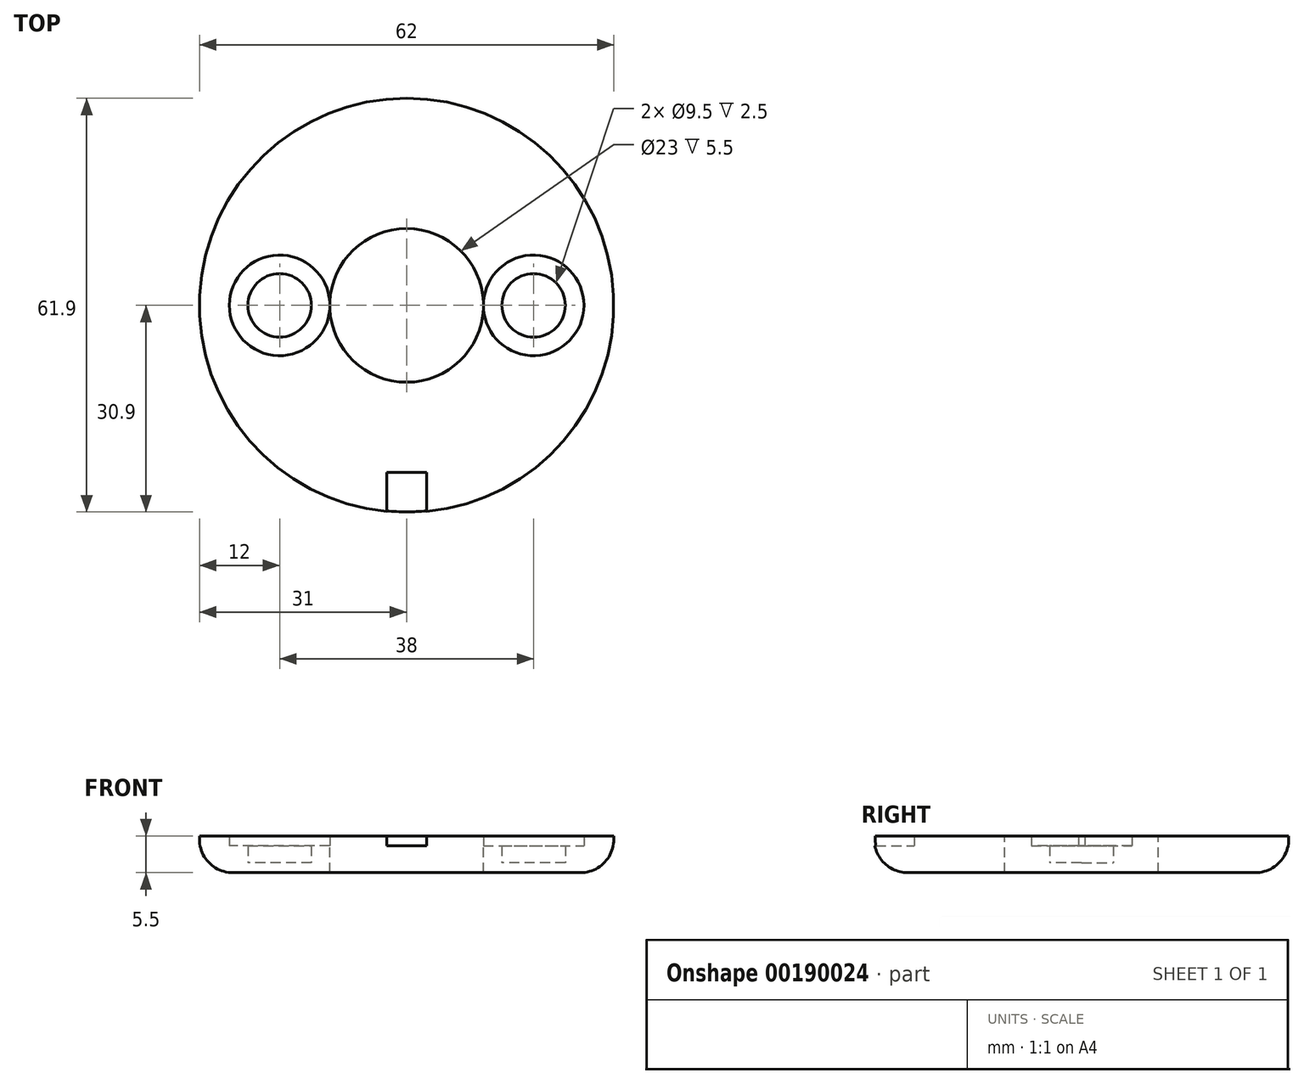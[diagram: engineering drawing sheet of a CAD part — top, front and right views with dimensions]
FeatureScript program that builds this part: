
annotation { "Feature Type Name" : "Feature", "Feature Type Description" : "" }
export const myFeature = defineFeature(function(context is Context, id is Id, definition is map)
    precondition{}
    {
        {
            var Q0;
            Q0=qCreatedBy(makeId("Top.planeOp"),FACE);
            var sketch = newSketch(context, id + "F0", { "sketchPlane" : qUnion([Q0])});
            skCircle(sketch, "E0", {"center": v(0, 0) * mm, "radius": 31 * mm});
            skLineSegment(sketch, "E1", {"start": v(-31, 0) * mm, "end": v(31, 0) * mm, "construction": true});
            skCircle(sketch, "E2", {"center": v(0, 0) * mm, "radius": 11.5 * mm});
            skSolve(sketch);
        }
        {
            var Q0;
            Q0=makeQuery(id+"F0.imprint","IMPRINT",FACE,{"disambiguationData":[TD([[makeQuery(id+"F0.imprint","IMPRINT",EDGE,{"derivedFrom":sQuery(id+"F0.wireOp",EDGE,"E0")}),1.0]])]});
            extrude(context, id + "F1", {"entities" : qUnion([Q0]), "oppositeDirection" : true, "depth" : 1.5 * mm});
        }
        {
            var Q0;
            Q0=makeQuery(id+"F1.opExtrude","CAP_FACE",FACE,{"disambiguationData":[OSD([sQuery(id+"F0.wireOp",EDGE,"E0"),sQuery(id+"F0.wireOp",EDGE,"E2")])],"isStart":false});
            var sketch = newSketch(context, id + "F2", { "sketchPlane" : qUnion([Q0])});
            skCircle(sketch, "E3.0", {"center": v(0, 0) * mm, "radius": 31 * mm});
            skCircle(sketch, "E4.0", {"center": v(0, 0) * mm, "radius": 11.5 * mm});
            skLineSegment(sketch, "E5.0", {"start": v(-31, 0) * mm, "end": v(31, 0) * mm, "construction": true});
            skPoint(sketch, "E6", {"position": v(-19, 0) * mm});
            skPoint(sketch, "E7", {"position": v(19, 0) * mm});
            skCircle(sketch, "E8", {"center": v(19, 0) * mm, "radius": 4.75 * mm});
            skCircle(sketch, "E9", {"center": v(-19, 0) * mm, "radius": 4.75 * mm});
            skSolve(sketch);
        }
        {
            var Q0;
            Q0=makeQuery(id+"F2.imprint","IMPRINT",FACE,{"disambiguationData":[TD([[makeQuery(id+"F2.imprint","IMPRINT",EDGE,{"derivedFrom":sQuery(id+"F2.wireOp",EDGE,"E3.0")}),-1.0]])]});
            extrude(context, id + "F3", {"entities" : qUnion([Q0]), "operationType" : NewBodyOperationType.ADD, "oppositeDirection" : true, "depth" : 4 * mm});
        }
        {
            var Q0;
            Q0=makeQuery(id+"F3.opExtrude","CAP_FACE",FACE,{"disambiguationData":[OSD([sQuery(id+"F2.wireOp",EDGE,"E3.0"),sQuery(id+"F2.wireOp",EDGE,"E4.0"),sQuery(id+"F2.wireOp",EDGE,"E8"),sQuery(id+"F2.wireOp",EDGE,"E9")])],"isStart":false});
            var sketch = newSketch(context, id + "F4", { "sketchPlane" : qUnion([Q0])});
            skCircle(sketch, "E10.0", {"center": v(0, 0) * mm, "radius": 31 * mm});
            skCircle(sketch, "E11.0", {"center": v(0, 0) * mm, "radius": 11.5 * mm});
            skPoint(sketch, "E12.0", {"position": v(-19, 0) * mm});
            skPoint(sketch, "E13.0", {"position": v(19, 0) * mm});
            skCircle(sketch, "E14", {"center": v(19, 0) * mm, "radius": 7.53 * mm});
            skCircle(sketch, "E15", {"center": v(-19, 0) * mm, "radius": 7.53 * mm});
            skLineSegment(sketch, "E16", {"start": v(0, 0) * mm, "end": v(0, -31) * mm, "construction": true});
            skLineSegment(sketch, "E17", {"start": v(-3, -30.85) * mm, "end": v(-3, -25) * mm});
            skLineSegment(sketch, "E18", {"start": v(-3, -25) * mm, "end": v(3, -25) * mm});
            skLineSegment(sketch, "E19", {"start": v(3, -25) * mm, "end": v(3, -30.85) * mm});
            skSolve(sketch);
        }
        {
            var Q0;
            {var subQ5=sQuery(id+"F4.wireOp",EDGE,"E17");Q0=makeQuery(id+"F4.imprint","IMPRINT",FACE,{"disambiguationData":[TD([[makeQuery(id+"F4.imprint","IMPRINT",EDGE,{"derivedFrom":subQ5}),1.0]])]});}
            extrude(context, id + "F5", {"entities" : qUnion([Q0]), "operationType" : NewBodyOperationType.ADD, "depth" : 1.5 * mm});
        }
        {
            var Q0;
            Q0=makeQuery(id+"F1.opExtrude","CAP_EDGE",EDGE,{"disambiguationData":[OSD([sQuery(id+"F0.wireOp",EDGE,"E0")])],"isStart":false});
            fillet(context, id + "F6", {"entities" : qUnion([Q0]), "radius" : 5 * mm, "tangentPropagation" : true, "allowEdgeOverflow" : false});
        }
    });
